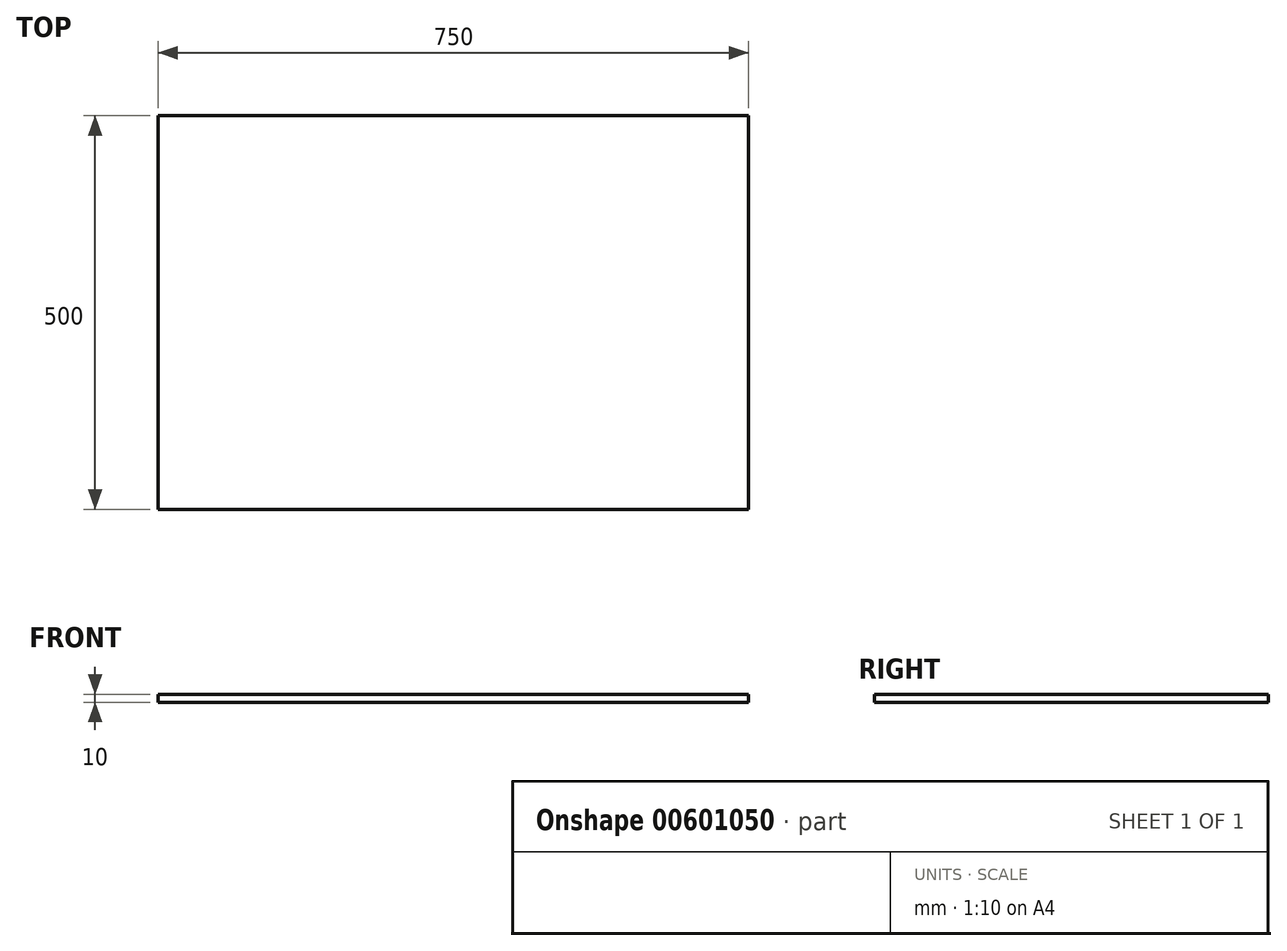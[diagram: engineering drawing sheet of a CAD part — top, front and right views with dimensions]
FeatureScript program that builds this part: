
annotation { "Feature Type Name" : "Feature", "Feature Type Description" : "" }
export const myFeature = defineFeature(function(context is Context, id is Id, definition is map)
    precondition{}
    {
        {
            var Q0;
            Q0=qCreatedBy(makeId("Top.planeOp"),FACE);
            var sketch = newSketch(context, id + "F0", { "sketchPlane" : qUnion([Q0])});
            skLineSegment(sketch, "E0.bottom", {"start": v(-523.3, 263.85) * mm, "end": v(226.7, 263.85) * mm});
            skLineSegment(sketch, "E0.top", {"start": v(-523.3, -236.15) * mm, "end": v(226.7, -236.15) * mm});
            skLineSegment(sketch, "E0.left", {"start": v(-523.3, 263.85) * mm, "end": v(-523.3, -236.15) * mm});
            skLineSegment(sketch, "E0.right", {"start": v(226.7, 263.85) * mm, "end": v(226.7, -236.15) * mm});
            skSolve(sketch);
        }
        {
            var Q0;
            Q0 = qSketchRegion(id + "F0", true);
            extrude(context, id + "F1", {"entities" : qUnion([Q0]), "depth" : 10 * mm, "offsetDistance" : 25 * mm});
        }
    });
